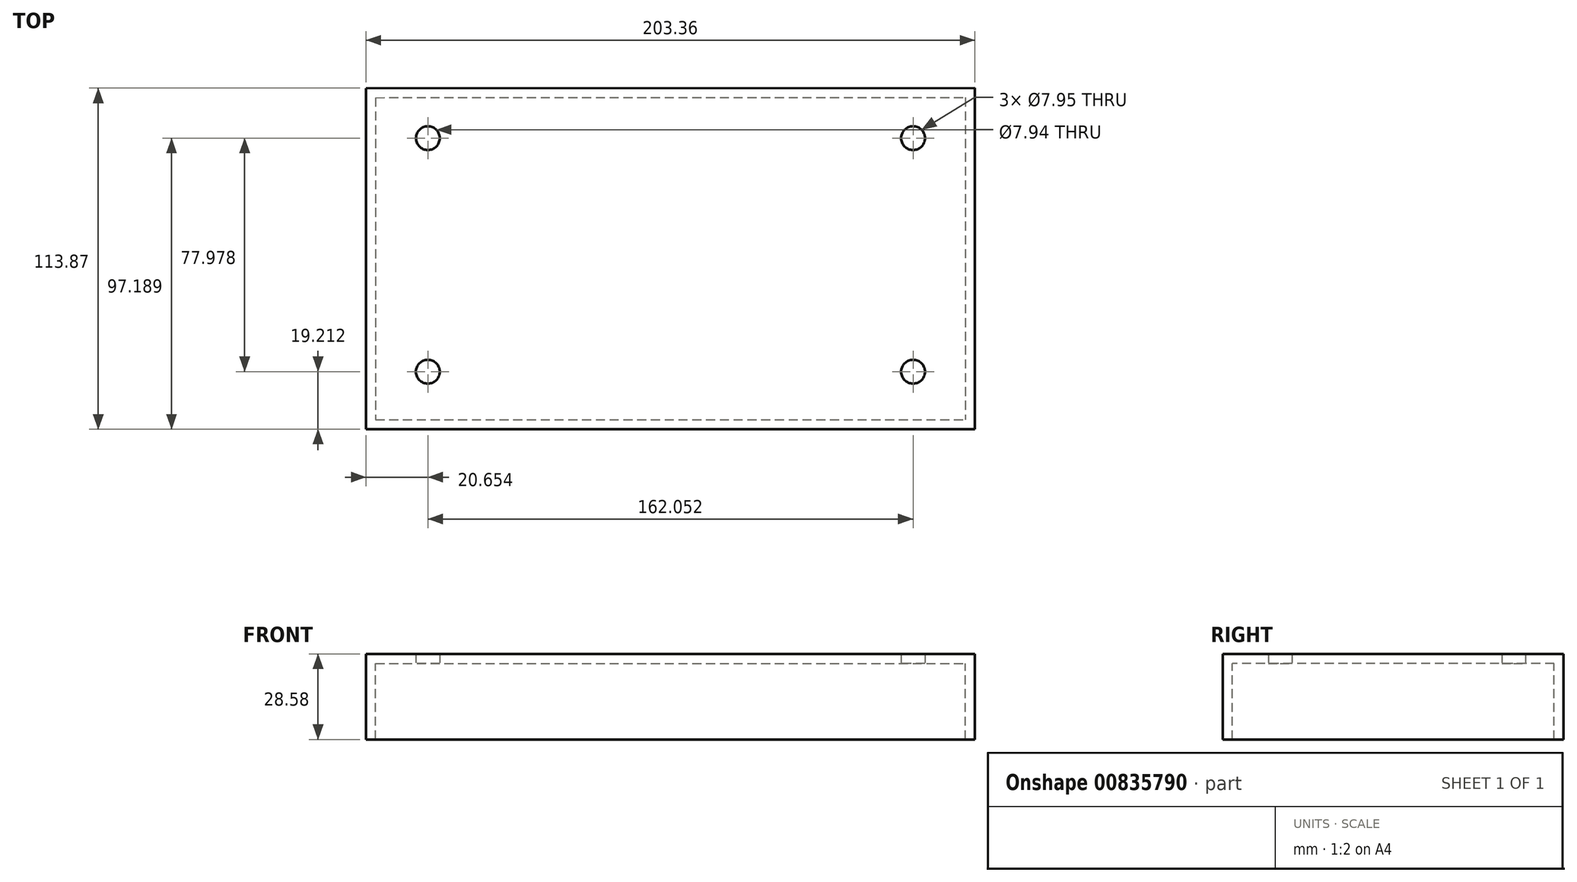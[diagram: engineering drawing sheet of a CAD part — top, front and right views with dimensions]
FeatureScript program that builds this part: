
annotation { "Feature Type Name" : "Feature", "Feature Type Description" : "" }
export const myFeature = defineFeature(function(context is Context, id is Id, definition is map)
    precondition{}
    {
        {
            var Q0;
            Q0=qCreatedBy(makeId("Top.planeOp"),FACE);
            var sketch = newSketch(context, id + "F0", { "sketchPlane" : qUnion([Q0])});
            skCircle(sketch, "E0", {"center": v(-82.34, -5.5) * mm, "radius": 3.97 * mm});
            skCircle(sketch, "E1", {"center": v(79.72, -5.5) * mm, "radius": 3.98 * mm});
            skLineSegment(sketch, "E2", {"start": v(-102.99, -102.7) * mm, "end": v(100.37, -102.7) * mm});
            skLineSegment(sketch, "E3", {"start": v(-102.99, 11.17) * mm, "end": v(-102.99, -102.7) * mm});
            skLineSegment(sketch, "E4", {"start": v(-102.99, 11.17) * mm, "end": v(100.37, 11.18) * mm});
            skLineSegment(sketch, "E5.MirrorCS", {"start": v(100.37, 11.18) * mm, "end": v(100.37, -102.7) * mm});
            skPoint(sketch, "E6.orphan", {"position": v(79.72, 11.17) * mm});
            skPoint(sketch, "E7.orphan", {"position": v(100.37, -5.5) * mm});
            skPoint(sketch, "E8.orphan", {"position": v(-82.34, 11.17) * mm});
            skPoint(sketch, "E9.orphan", {"position": v(-102.99, -5.5) * mm});
            skPoint(sketch, "E10.orphan", {"position": v(-102.99, -86.02) * mm});
            skPoint(sketch, "E11.orphan", {"position": v(100.37, -86.01) * mm});
            skCircle(sketch, "E12", {"center": v(79.72, -83.48) * mm, "radius": 3.98 * mm});
            skCircle(sketch, "E13", {"center": v(-82.34, -83.48) * mm, "radius": 3.98 * mm});
            skSolve(sketch);
        }
        {
            var Q0;
            Q0=makeQuery(id+"F0.imprint","IMPRINT",FACE,{"disambiguationData":[TD([[makeQuery(id+"F0.imprint","IMPRINT",EDGE,{"derivedFrom":sQuery(id+"F0.wireOp",EDGE,"E0")}),-1.0]])]});
            extrude(context, id + "F1", {"entities" : qUnion([Q0]), "depth" : 3.17 * mm, "offsetDistance" : 25.4 * mm});
        }
        {
            var Q0;
            Q0=makeQuery(id+"F1.opExtrude","CAP_FACE",FACE,{"disambiguationData":[OSD([sQuery(id+"F0.wireOp",EDGE,"E0"),sQuery(id+"F0.wireOp",EDGE,"E1"),sQuery(id+"F0.wireOp",EDGE,"peKi82K9-KoGG-puZw-5l8X-7xDcEHp8Ydru"),sQuery(id+"F0.wireOp",EDGE,"xWbMy6ly-FA9U-Xhqo-oOwH-LanU4p7uEBTC"),sQuery(id+"F0.wireOp",EDGE,"T1ZjZT7j-pke5-BZ06-akLB-1txo3vhOJwFk"),sQuery(id+"F0.wireOp",EDGE,"gq8HDo5O-rfG2-GLhP-j1gu-QqSE1rA41nlp"),sQuery(id+"F0.wireOp",EDGE,"eCUFU1Bq-wYZB-nymo-s4Oo-KepNOb2CuQL7"),sQuery(id+"F0.wireOp",EDGE,"Tp5xqSLA-fHft-Sy7i-IXtV-DoXRgNH4XesE"),sQuery(id+"F0.wireOp",EDGE,"n0KwhmgC-95xZ-sfZf-FitX-VjjL97is0wof"),sQuery(id+"F0.wireOp",EDGE,"Jjj8KEdg-SKrN-B9fX-I5cZ-AAn31WZU0f0g"),sQuery(id+"F0.wireOp",EDGE,"E2"),sQuery(id+"F0.wireOp",EDGE,"E3"),sQuery(id+"F0.wireOp",EDGE,"E4"),sQuery(id+"F0.wireOp",EDGE,"E5.MirrorCS")])],"isStart":true});
            var sketch = newSketch(context, id + "F2", { "sketchPlane" : qUnion([Q0])});
            skLineSegment(sketch, "E14.0", {"start": v(-102.99, 102.7) * mm, "end": v(100.37, 102.7) * mm});
            skLineSegment(sketch, "E14.1", {"start": v(-102.99, -11.17) * mm, "end": v(-102.99, 102.7) * mm});
            skLineSegment(sketch, "E14.2", {"start": v(-102.99, -11.17) * mm, "end": v(100.37, -11.18) * mm});
            skLineSegment(sketch, "E14.3", {"start": v(100.37, -11.18) * mm, "end": v(100.37, 102.7) * mm});
            skLineSegment(sketch, "E15.0", {"start": v(-99.81, 99.52) * mm, "end": v(97.2, 99.52) * mm});
            skLineSegment(sketch, "E15.1", {"start": v(-99.81, -8) * mm, "end": v(-99.81, 99.52) * mm});
            skLineSegment(sketch, "E15.2", {"start": v(-99.81, -8) * mm, "end": v(97.2, -8) * mm});
            skLineSegment(sketch, "E15.3", {"start": v(97.2, -8) * mm, "end": v(97.2, 99.52) * mm});
            skLineSegment(sketch, "E16.0", {"start": v(106.72, -17.53) * mm, "end": v(106.73, 109.04) * mm});
            skLineSegment(sketch, "E16.1", {"start": v(-109.34, -17.52) * mm, "end": v(106.72, -17.53) * mm});
            skLineSegment(sketch, "E16.2", {"start": v(-109.34, 109.04) * mm, "end": v(-109.34, -17.52) * mm});
            skLineSegment(sketch, "E16.3", {"start": v(106.73, 109.04) * mm, "end": v(-109.34, 109.04) * mm});
            skSolve(sketch);
        }
        {
            var Q0;
            Q0=makeQuery(id+"F2.imprint","IMPRINT",FACE,{"disambiguationData":[TD([[makeQuery(id+"F2.imprint","IMPRINT",EDGE,{"derivedFrom":sQuery(id+"F2.wireOp",EDGE,"E14.0")}),-1.0]])]});
            extrude(context, id + "F3", {"entities" : qUnion([Q0]), "operationType" : NewBodyOperationType.ADD, "depth" : 25.4 * mm, "offsetDistance" : 25.4 * mm});
        }
    });
